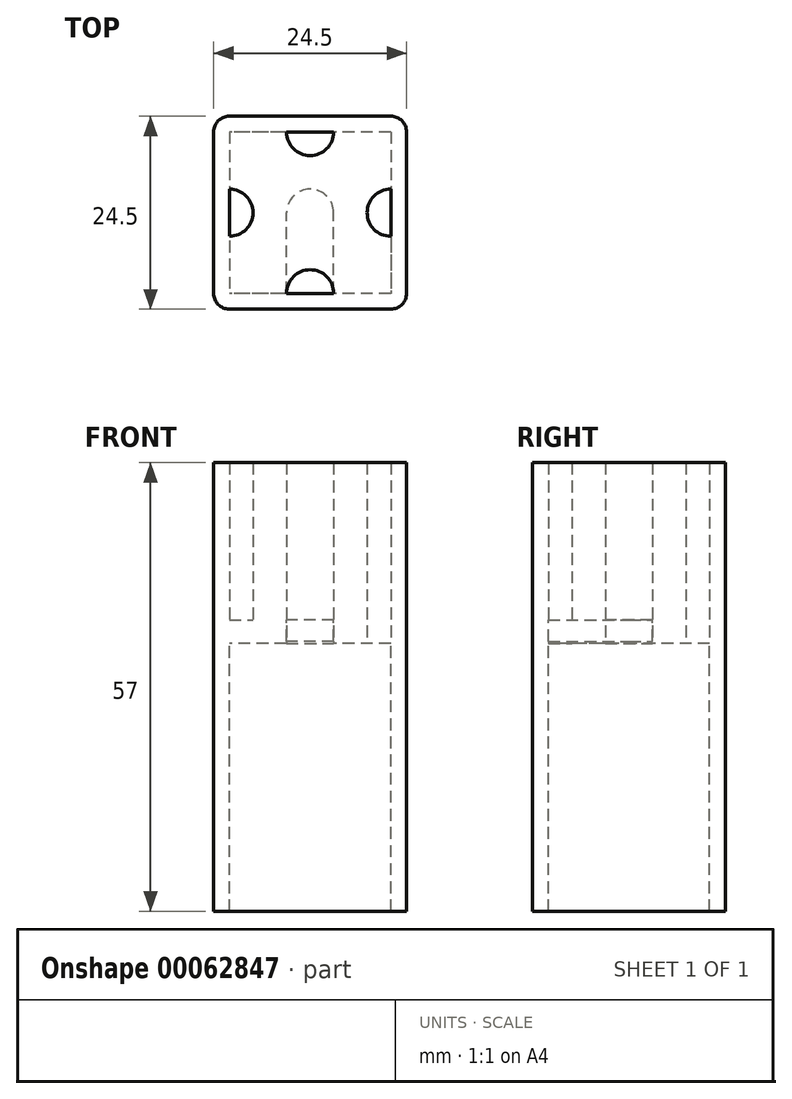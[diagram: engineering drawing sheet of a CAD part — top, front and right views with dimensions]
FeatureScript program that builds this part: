
annotation { "Feature Type Name" : "Feature", "Feature Type Description" : "" }
export const myFeature = defineFeature(function(context is Context, id is Id, definition is map)
    precondition{}
    {
        {
            var Q0;
            Q0=qCreatedBy(makeId("Top.planeOp"),FACE);
            var sketch = newSketch(context, id + "F0", { "sketchPlane" : qUnion([Q0])});
            skLineSegment(sketch, "E0.rect.bottom", {"start": v(10.25, -10.25) * mm, "end": v(-10.25, -10.25) * mm});
            skLineSegment(sketch, "E0.rect.top", {"start": v(10.25, 10.25) * mm, "end": v(-10.25, 10.25) * mm});
            skLineSegment(sketch, "E0.rect.left", {"start": v(10.25, -10.25) * mm, "end": v(10.25, 10.25) * mm});
            skLineSegment(sketch, "E0.rect.right", {"start": v(-10.25, -10.25) * mm, "end": v(-10.25, 10.25) * mm});
            skPoint(sketch, "E0.rect.middle", {"position": v(0, 0) * mm});
            skLineSegment(sketch, "E1.0", {"start": v(12.25, 12.25) * mm, "end": v(-12.25, 12.25) * mm});
            skLineSegment(sketch, "E1.1", {"start": v(12.25, -12.25) * mm, "end": v(12.25, 12.25) * mm});
            skLineSegment(sketch, "E1.2", {"start": v(12.25, -12.25) * mm, "end": v(-12.25, -12.25) * mm});
            skLineSegment(sketch, "E1.3", {"start": v(-12.25, -12.25) * mm, "end": v(-12.25, 12.25) * mm});
            skArc(sketch, "E2", {"start": v(-10.25, 3) * mm, "mid": v(-7.25, 0) * mm, "end": v(-10.25, -3) * mm});
            skArc(sketch, "E3", {"start": v(-3, -10.25) * mm, "mid": v(0, -7.25) * mm, "end": v(3, -10.25) * mm});
            skArc(sketch, "E4", {"start": v(10.25, -3) * mm, "mid": v(7.25, 0) * mm, "end": v(10.25, 3) * mm});
            skArc(sketch, "E5", {"start": v(-3, 10.25) * mm, "mid": v(0, 7.25) * mm, "end": v(3, 10.25) * mm});
            skSolve(sketch);
        }
        {
            var Q0;
            Q0=makeQuery(id+"F0.imprint","IMPRINT",FACE,{"disambiguationData":[TD([[makeQuery(id+"F0.imprint","IMPRINT",EDGE,{"derivedFrom":sQuery(id+"F0.wireOp",EDGE,"E1.0")}),1.0]])]});
            extrude(context, id + "F1", {"entities" : qUnion([Q0]), "depth" : 37 * mm});
        }
        {
            var Q0;
            {var subQ0=sQuery(id+"F0.wireOp",EDGE,"E3");Q0=makeQuery(id+"F0.imprint","IMPRINT",FACE,{"disambiguationData":[TD([[makeQuery(id+"F0.imprint","IMPRINT",EDGE,{"derivedFrom":subQ0}),-1.0]])]});}
            var Q1;
            {var subQ0=sQuery(id+"F0.wireOp",EDGE,"E2");Q1=makeQuery(id+"F0.imprint","IMPRINT",FACE,{"disambiguationData":[TD([[makeQuery(id+"F0.imprint","IMPRINT",EDGE,{"derivedFrom":subQ0}),-1.0]])]});}
            var Q2;
            {var subQ0=sQuery(id+"F0.wireOp",EDGE,"E4");Q2=makeQuery(id+"F0.imprint","IMPRINT",FACE,{"disambiguationData":[TD([[makeQuery(id+"F0.imprint","IMPRINT",EDGE,{"derivedFrom":subQ0}),-1.0]])]});}
            var Q3;
            Q3=makeQuery(id+"F0.imprint","IMPRINT",FACE,{"disambiguationData":[TD([[makeQuery(id+"F0.imprint","IMPRINT",EDGE,{"derivedFrom":sQuery(id+"F0.wireOp",EDGE,"E1.0")}),1.0]])]});
            extrude(context, id + "F2", {"entities" : qUnion([Q0, Q1, Q2, Q3]), "operationType" : NewBodyOperationType.ADD, "oppositeDirection" : true, "depth" : 20 * mm});
        }
        {
            var Q0;
            {var subQ3=sQuery(id+"F0.wireOp",EDGE,"E2");Q0=makeQuery(id+"F0.imprint","IMPRINT",FACE,{"disambiguationData":[TD([[makeQuery(id+"F0.imprint","IMPRINT",EDGE,{"derivedFrom":subQ3}),1.0]])]});}
            var Q1;
            {var subQ0=sQuery(id+"F0.wireOp",EDGE,"E2");Q1=makeQuery(id+"F0.imprint","IMPRINT",FACE,{"disambiguationData":[TD([[makeQuery(id+"F0.imprint","IMPRINT",EDGE,{"derivedFrom":subQ0}),-1.0]])]});}
            var Q2;
            {var subQ0=sQuery(id+"F0.wireOp",EDGE,"E3");Q2=makeQuery(id+"F0.imprint","IMPRINT",FACE,{"disambiguationData":[TD([[makeQuery(id+"F0.imprint","IMPRINT",EDGE,{"derivedFrom":subQ0}),-1.0]])]});}
            var Q3;
            {var subQ0=sQuery(id+"F0.wireOp",EDGE,"E4");Q3=makeQuery(id+"F0.imprint","IMPRINT",FACE,{"disambiguationData":[TD([[makeQuery(id+"F0.imprint","IMPRINT",EDGE,{"derivedFrom":subQ0}),-1.0]])]});}
            extrude(context, id + "F3", {"entities" : qUnion([Q0, Q1, Q2, Q3]), "operationType" : NewBodyOperationType.ADD, "depth" : 3 * mm});
        }
        {
            var Q0;
            Q0=makeQuery(id+"F3.opExtrude","CAP_FACE",FACE,{"disambiguationData":[OSD([sQuery(id+"F0.wireOp",EDGE,"E0.rect.bottom"),sQuery(id+"F0.wireOp",EDGE,"E0.rect.top"),sQuery(id+"F0.wireOp",EDGE,"E0.rect.left"),sQuery(id+"F0.wireOp",EDGE,"E0.rect.right"),sQuery(id+"F0.wireOp",EDGE,"E5")])],"isStart":true});
            var sketch = newSketch(context, id + "F4", { "sketchPlane" : qUnion([Q0])});
            skCircle(sketch, "E6", {"center": v(0, 0) * mm, "radius": 3 * mm});
            skLineSegment(sketch, "E7", {"start": v(-3, -10.25) * mm, "end": v(-3, 0) * mm});
            skLineSegment(sketch, "E8", {"start": v(3, -10.25) * mm, "end": v(3, 0) * mm});
            skLineSegment(sketch, "E9", {"start": v(-3, -10.25) * mm, "end": v(3, -10.25) * mm});
            skSolve(sketch);
        }
        {
            var Q0;
            {var subQ0=sQuery(id+"F4.wireOp",EDGE,"E7");var subQ1=sQuery(id+"F4.wireOp",EDGE,"E6");var subQ2=makeQuery(id+"F4.imprint","INTERSECT",VERTEX,{"derivedFrom":[subQ1,subQ0]});Q0=makeQuery(id+"F4.imprint","IMPRINT",FACE,{"disambiguationData":[TD([[makeQuery(id+"F4.imprint","IMPRINT",EDGE,{"disambiguationData":[TD([[subQ2,-1.0]])],"derivedFrom":subQ1}),-1.0]])]});}
            var Q1;
            {var subQ0=sQuery(id+"F4.wireOp",EDGE,"E6");var subQ1=makeQuery(id+"F4.imprint","INTERSECT",VERTEX,{"derivedFrom":[subQ0,sQuery(id+"F4.wireOp",EDGE,"E7")]});Q1=makeQuery(id+"F4.imprint","IMPRINT",FACE,{"disambiguationData":[TD([[makeQuery(id+"F4.imprint","IMPRINT",EDGE,{"disambiguationData":[TD([[subQ1,1.0]])],"derivedFrom":subQ0}),1.0]])]});}
            extrude(context, id + "F5", {"entities" : qUnion([Q0, Q1]), "operationType" : NewBodyOperationType.REMOVE, "oppositeDirection" : true, "depth" : 2.7 * mm});
        }
        {
            var Q0;
            {var subQ0=sQuery(id+"F0.wireOp",EDGE,"E1.3");var subQ1=sQuery(id+"F0.wireOp",EDGE,"E1.2");Q0=makeQuery(id+"F2.boolean.opBoolean","MERGE",EDGE,{"derivedFrom":[makeQuery(id+"F1.opExtrude","SWEPT_EDGE",EDGE,{"disambiguationData":[OSD([subQ1,subQ0])]}),makeQuery(id+"F2.opExtrude","SWEPT_EDGE",EDGE,{"disambiguationData":[OSD([subQ1,subQ0])]})]});}
            var Q1;
            {var subQ0=sQuery(id+"F0.wireOp",EDGE,"E1.2");var subQ1=sQuery(id+"F0.wireOp",EDGE,"E1.1");Q1=makeQuery(id+"F2.boolean.opBoolean","MERGE",EDGE,{"derivedFrom":[makeQuery(id+"F1.opExtrude","SWEPT_EDGE",EDGE,{"disambiguationData":[OSD([subQ1,subQ0])]}),makeQuery(id+"F2.opExtrude","SWEPT_EDGE",EDGE,{"disambiguationData":[OSD([subQ1,subQ0])]})]});}
            var Q2;
            {var subQ0=sQuery(id+"F0.wireOp",EDGE,"E1.1");var subQ1=sQuery(id+"F0.wireOp",EDGE,"E1.0");Q2=makeQuery(id+"F2.boolean.opBoolean","MERGE",EDGE,{"derivedFrom":[makeQuery(id+"F1.opExtrude","SWEPT_EDGE",EDGE,{"disambiguationData":[OSD([subQ1,subQ0])]}),makeQuery(id+"F2.opExtrude","SWEPT_EDGE",EDGE,{"disambiguationData":[OSD([subQ1,subQ0])]})]});}
            var Q3;
            {var subQ0=sQuery(id+"F0.wireOp",EDGE,"E1.3");var subQ1=sQuery(id+"F0.wireOp",EDGE,"E1.0");Q3=makeQuery(id+"F2.boolean.opBoolean","MERGE",EDGE,{"derivedFrom":[makeQuery(id+"F1.opExtrude","SWEPT_EDGE",EDGE,{"disambiguationData":[OSD([subQ1,subQ0])]}),makeQuery(id+"F2.opExtrude","SWEPT_EDGE",EDGE,{"disambiguationData":[OSD([subQ1,subQ0])]})]});}
            fillet(context, id + "F6", {"entities" : qUnion([Q0, Q1, Q2, Q3]), "radius" : 2 * mm, "tangentPropagation" : true, "allowEdgeOverflow" : false});
        }
        {
            var Q0;
            Q0=makeQuery(id+"F1.opExtrude","SWEPT_BODY",BODY,{"disambiguationData":[OSD([sQuery(id+"F0.wireOp",EDGE,"E0.rect.bottom"),sQuery(id+"F0.wireOp",EDGE,"E0.rect.top"),sQuery(id+"F0.wireOp",EDGE,"E0.rect.left"),sQuery(id+"F0.wireOp",EDGE,"E0.rect.right"),sQuery(id+"F0.wireOp",EDGE,"E1.0"),sQuery(id+"F0.wireOp",EDGE,"E1.1"),sQuery(id+"F0.wireOp",EDGE,"E1.2"),sQuery(id+"F0.wireOp",EDGE,"E1.3")])]});
            var Q1;
            Q1=makeQuery(id+"F1.opExtrude","CAP_EDGE",EDGE,{"disambiguationData":[OSD([sQuery(id+"F0.wireOp",EDGE,"E1.2")])],"isStart":false});
            transform(context, id + "F7", {"entities" : qUnion([Q0]), "transformType" : TransformType.ROTATION, "transformAxis" : qUnion([Q1]), "angle" : 180 * degree, "oppositeDirection" : true, "makeCopy" : false});
        }
    });
